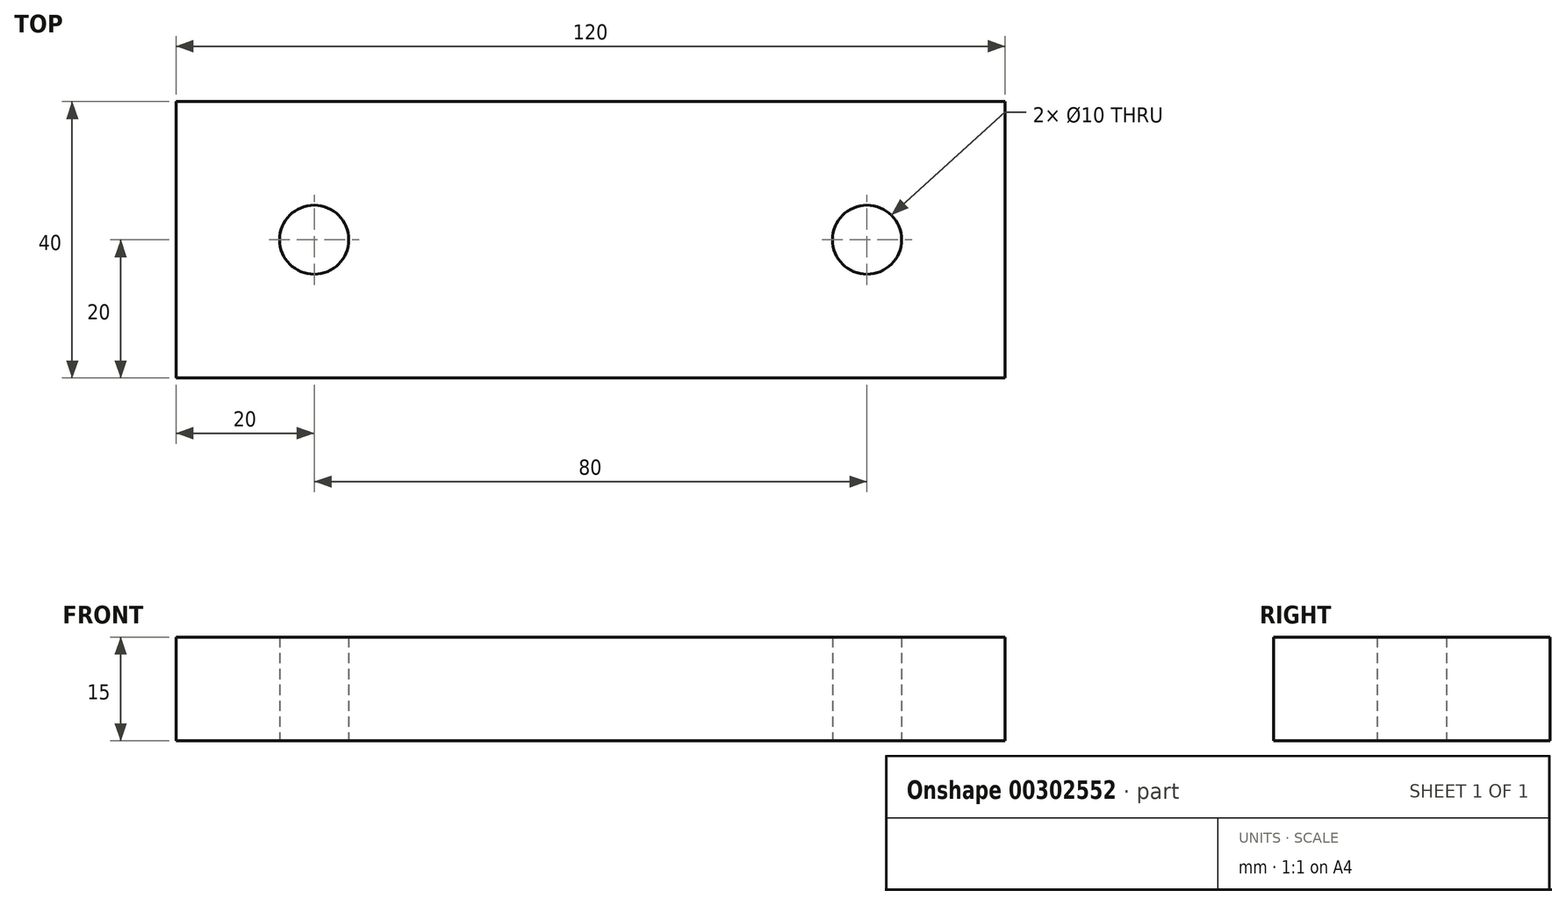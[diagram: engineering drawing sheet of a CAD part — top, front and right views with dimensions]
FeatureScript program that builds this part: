
annotation { "Feature Type Name" : "Feature", "Feature Type Description" : "" }
export const myFeature = defineFeature(function(context is Context, id is Id, definition is map)
    precondition{}
    {
        {
            var Q0;
            Q0=qCreatedBy(makeId("Top.planeOp"),FACE);
            var sketch = newSketch(context, id + "F0", { "sketchPlane" : qUnion([Q0])});
            skLineSegment(sketch, "E0.bottom", {"start": v(0, 0) * mm, "end": v(120, 0) * mm});
            skLineSegment(sketch, "E0.top", {"start": v(0, -40) * mm, "end": v(120, -40) * mm});
            skLineSegment(sketch, "E0.left", {"start": v(0, 0) * mm, "end": v(0, -40) * mm});
            skLineSegment(sketch, "E0.right", {"start": v(120, 0) * mm, "end": v(120, -40) * mm});
            skCircle(sketch, "E1", {"center": v(100, -20) * mm, "radius": 5 * mm});
            skCircle(sketch, "E2", {"center": v(20, -20) * mm, "radius": 5 * mm});
            skSolve(sketch);
        }
        {
            var Q0;
            Q0 = qSketchRegion(id + "F0", true);
            extrude(context, id + "F1", {"entities" : qUnion([Q0]), "depth" : 15 * mm});
        }
    });
